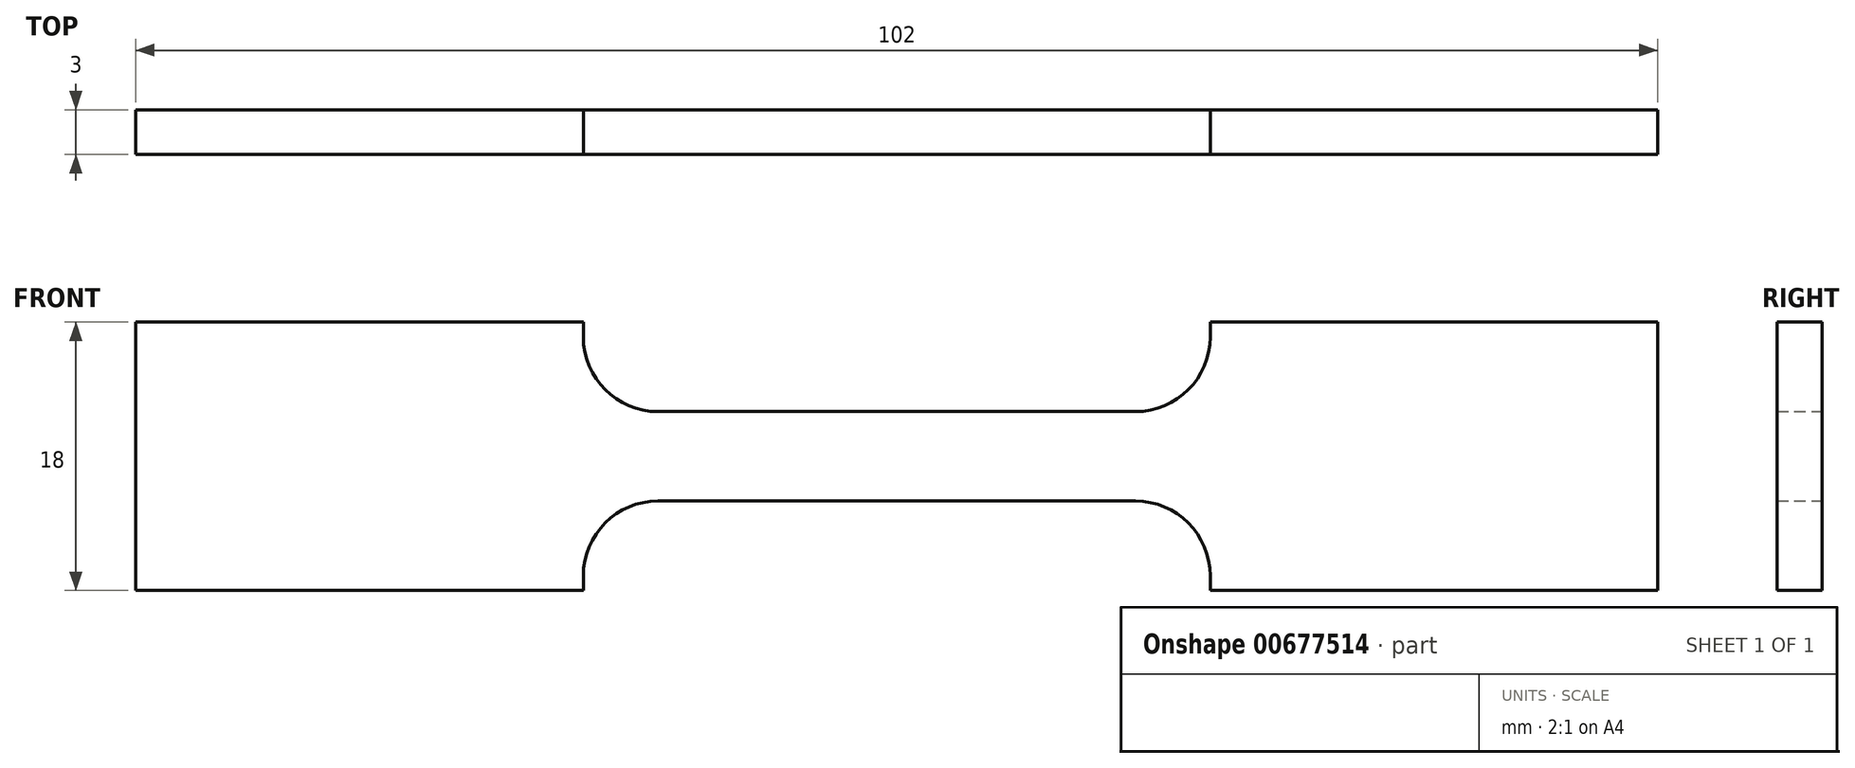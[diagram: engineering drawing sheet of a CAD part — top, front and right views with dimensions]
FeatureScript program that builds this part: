
annotation { "Feature Type Name" : "Feature", "Feature Type Description" : "" }
export const myFeature = defineFeature(function(context is Context, id is Id, definition is map)
    precondition{}
    {
        {
            var Q0;
            Q0=qCreatedBy(makeId("Front.planeOp"),FACE);
            var sketch = newSketch(context, id + "F0", { "sketchPlane" : qUnion([Q0])});
            skLineSegment(sketch, "E0", {"start": v(-49.16, 10.93) * mm, "end": v(-49.16, 1.93) * mm});
            skLineSegment(sketch, "E1", {"start": v(-49.16, 1.93) * mm, "end": v(-19.16, 1.93) * mm});
            skLineSegment(sketch, "E2", {"start": v(22.84, 1.93) * mm, "end": v(52.84, 1.93) * mm});
            skLineSegment(sketch, "E3", {"start": v(52.84, 1.93) * mm, "end": v(52.84, 10.93) * mm});
            skLineSegment(sketch, "E4", {"start": v(-14.16, 7.93) * mm, "end": v(17.84, 7.93) * mm});
            skArc(sketch, "E5.MirrorCS", {"start": v(-14.16, 7.93) * mm, "mid": v(-17.7, 6.47) * mm, "end": v(-19.16, 2.93) * mm});
            skArc(sketch, "E6.MirrorCS", {"start": v(17.84, 7.93) * mm, "mid": v(21.38, 6.47) * mm, "end": v(22.84, 2.93) * mm});
            skPoint(sketch, "E7.orphan", {"position": v(-49.16, 19.93) * mm});
            skPoint(sketch, "E8.orphan", {"position": v(52.84, 19.93) * mm});
            skLineSegment(sketch, "E9", {"start": v(-19.16, 1.93) * mm, "end": v(-19.16, 2.93) * mm});
            skLineSegment(sketch, "E10", {"start": v(22.84, 1.93) * mm, "end": v(22.84, 2.93) * mm});
            skLineSegment(sketch, "E11.MirrorCS", {"start": v(22.84, 19.93) * mm, "end": v(22.84, 18.93) * mm});
            skLineSegment(sketch, "E12.MirrorCS", {"start": v(-19.16, 19.93) * mm, "end": v(-19.16, 18.93) * mm});
            skLineSegment(sketch, "E13.MirrorCS", {"start": v(52.84, 19.93) * mm, "end": v(52.84, 10.93) * mm});
            skLineSegment(sketch, "E14.MirrorCS", {"start": v(-49.16, 10.93) * mm, "end": v(-49.16, 19.93) * mm});
            skLineSegment(sketch, "E15.MirrorCS", {"start": v(-49.16, 19.93) * mm, "end": v(-19.16, 19.93) * mm});
            skLineSegment(sketch, "E16.MirrorCS", {"start": v(22.84, 19.93) * mm, "end": v(52.84, 19.93) * mm});
            skLineSegment(sketch, "E17.MirrorCS", {"start": v(-14.16, 13.93) * mm, "end": v(17.84, 13.93) * mm});
            skArc(sketch, "E18.MirrorCS", {"start": v(17.84, 13.93) * mm, "mid": v(21.38, 15.4) * mm, "end": v(22.84, 18.93) * mm});
            skArc(sketch, "E19.MirrorCS", {"start": v(-14.16, 13.93) * mm, "mid": v(-17.7, 15.4) * mm, "end": v(-19.16, 18.93) * mm});
            skSolve(sketch);
        }
        {
            var Q0;
            Q0=makeQuery(id+"F0.imprint","IMPRINT",FACE,{"disambiguationData":[TD([[makeQuery(id+"F0.imprint","IMPRINT",EDGE,{"derivedFrom":sQuery(id+"F0.wireOp",EDGE,"E0")}),1.0]])]});
            extrude(context, id + "F1", {"entities" : qUnion([Q0]), "depth" : 3 * mm, "offsetDistance" : 25 * mm});
        }
    });
